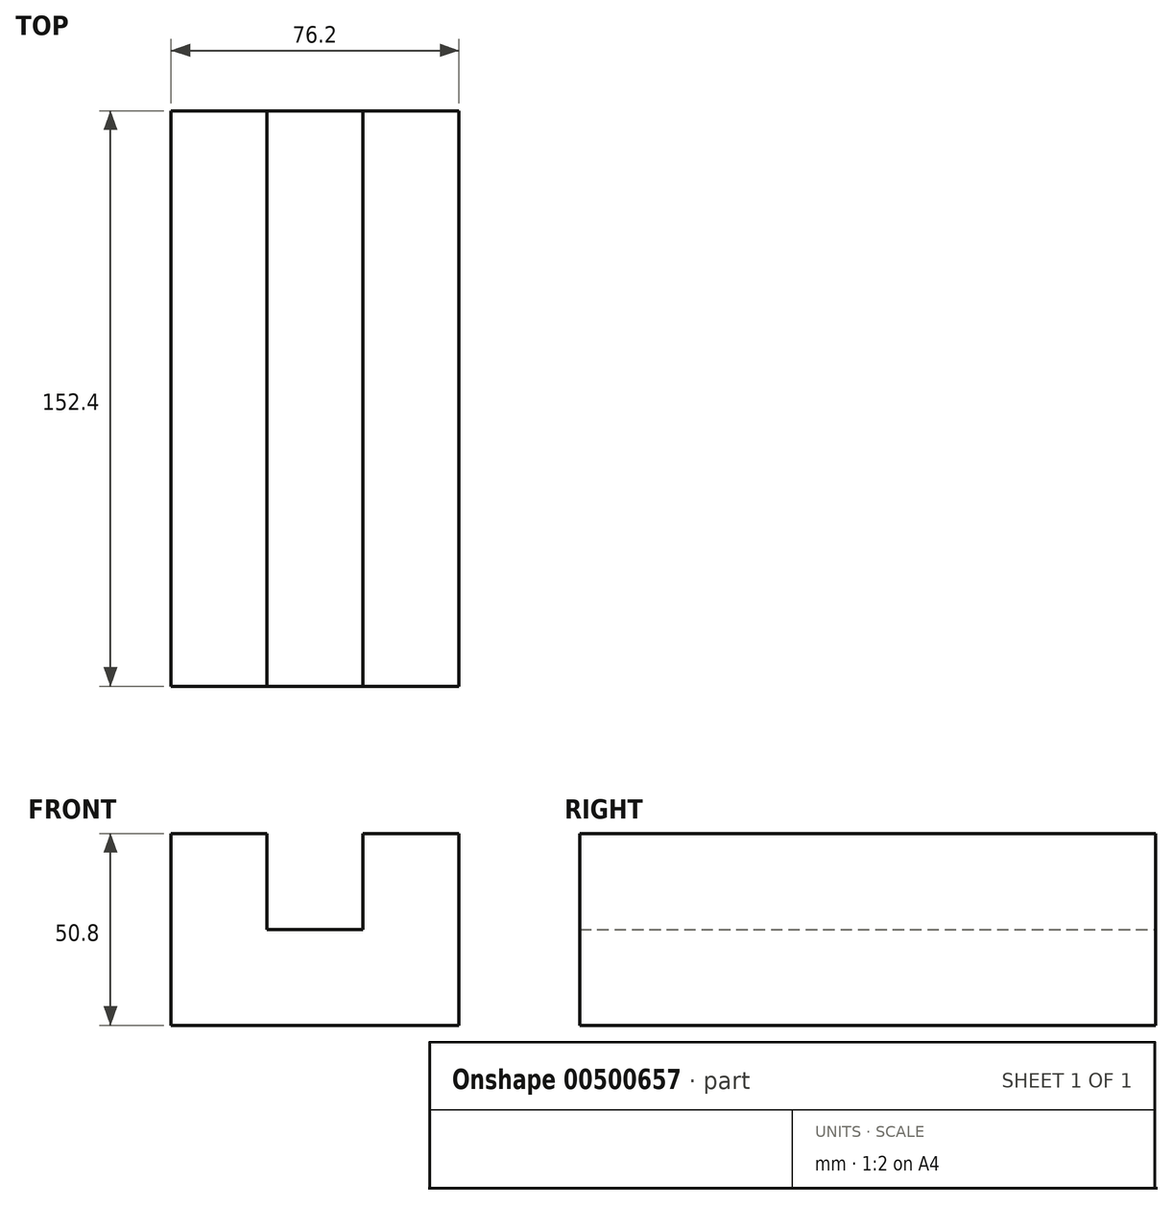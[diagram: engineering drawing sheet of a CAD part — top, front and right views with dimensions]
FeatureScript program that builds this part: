
annotation { "Feature Type Name" : "Feature", "Feature Type Description" : "" }
export const myFeature = defineFeature(function(context is Context, id is Id, definition is map)
    precondition{}
    {
        {
            var Q0;
            Q0=qCreatedBy(makeId("Front.planeOp"),FACE);
            var sketch = newSketch(context, id + "F0", { "sketchPlane" : qUnion([Q0])});
            skLineSegment(sketch, "E0", {"start": v(-28.64, 33.65) * mm, "end": v(-28.64, -17.15) * mm});
            skLineSegment(sketch, "E1", {"start": v(-28.64, -17.15) * mm, "end": v(47.56, -17.15) * mm});
            skLineSegment(sketch, "E2", {"start": v(47.56, -17.15) * mm, "end": v(47.56, 33.65) * mm});
            skLineSegment(sketch, "E3", {"start": v(47.56, 33.65) * mm, "end": v(22.16, 33.65) * mm});
            skLineSegment(sketch, "E4", {"start": v(22.16, 33.65) * mm, "end": v(22.16, 8.25) * mm});
            skLineSegment(sketch, "E5", {"start": v(22.16, 8.25) * mm, "end": v(-3.24, 8.25) * mm});
            skLineSegment(sketch, "E6", {"start": v(-3.24, 8.25) * mm, "end": v(-3.24, 33.65) * mm});
            skLineSegment(sketch, "E7", {"start": v(-3.24, 33.65) * mm, "end": v(-28.64, 33.65) * mm});
            skSolve(sketch);
        }
        {
            var Q0;
            Q0 = qSketchRegion(id + "F0", true);
            extrude(context, id + "F1", {"entities" : qUnion([Q0]), "depth" : 152.4 * mm});
        }
    });
